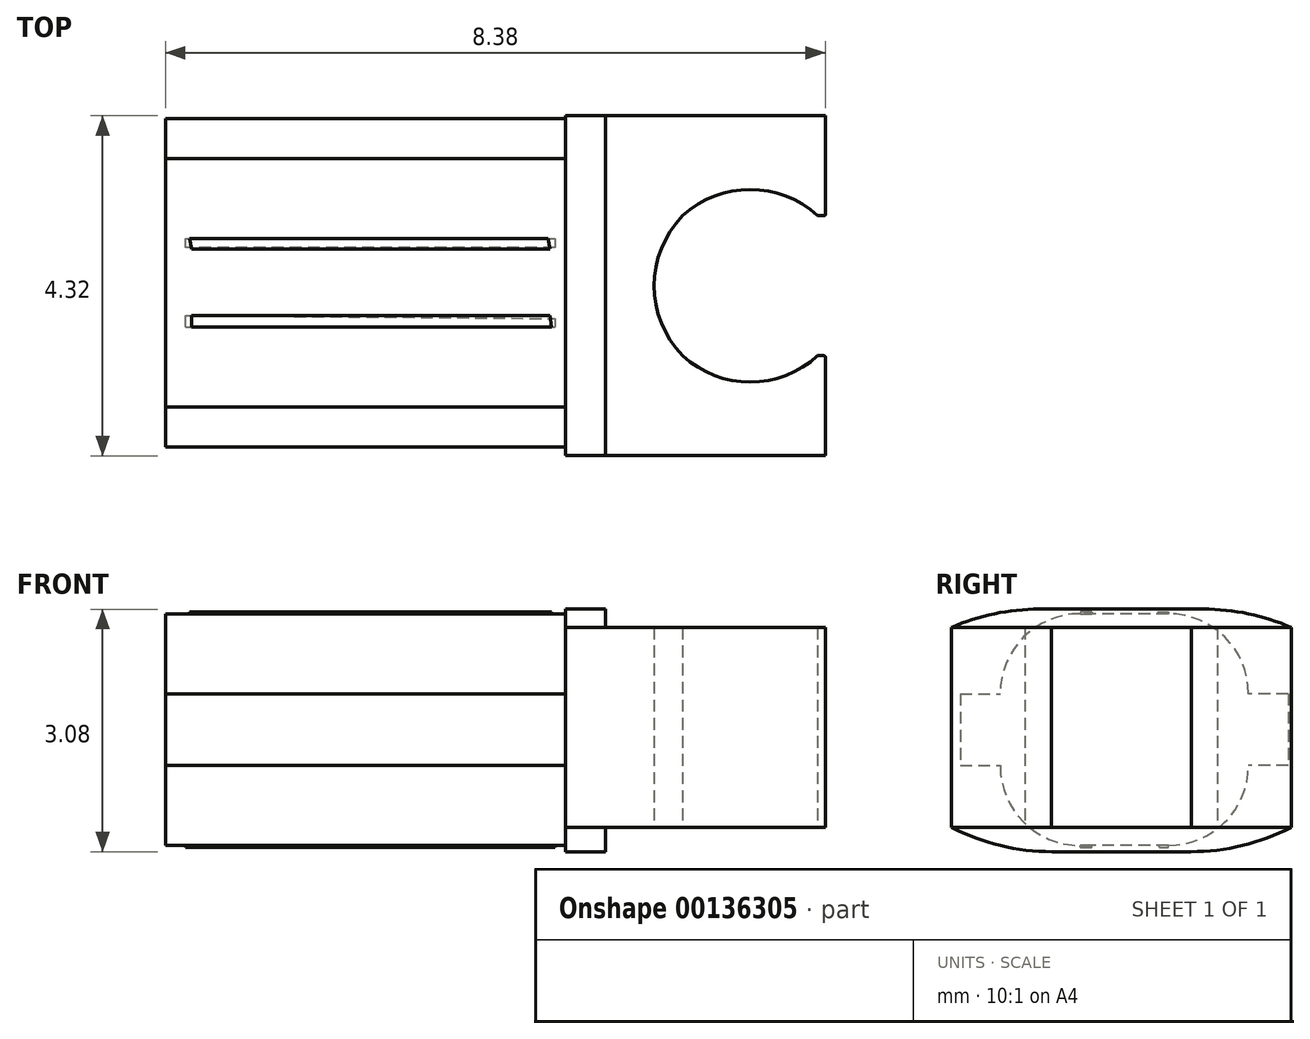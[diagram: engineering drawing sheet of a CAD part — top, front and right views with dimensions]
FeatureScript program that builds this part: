
annotation { "Feature Type Name" : "Feature", "Feature Type Description" : "" }
export const myFeature = defineFeature(function(context is Context, id is Id, definition is map)
    precondition{}
    {
        {
            var Q0;
            Q0=qCreatedBy(makeId("Top.planeOp"),FACE);
            var sketch = newSketch(context, id + "F0", { "sketchPlane" : qUnion([Q0])});
            skLineSegment(sketch, "E0", {"start": v(-1.88, 2.16) * mm, "end": v(0.91, 2.16) * mm});
            skLineSegment(sketch, "E1", {"start": v(-1.88, -2.16) * mm, "end": v(0.91, -2.16) * mm});
            skLineSegment(sketch, "E2", {"start": v(-1.88, 2.16) * mm, "end": v(-1.88, -2.16) * mm});
            skArc(sketch, "E3", {"start": v(-0.9, 0.89) * mm, "mid": v(-1.26, 0) * mm, "end": v(-0.9, -0.89) * mm});
            skLineSegment(sketch, "E4", {"start": v(0.91, -2.16) * mm, "end": v(0.91, -0.89) * mm});
            skArc(sketch, "E5", {"start": v(0.81, 0.89) * mm, "mid": v(-0.04, 1.22) * mm, "end": v(-0.9, 0.89) * mm});
            skArc(sketch, "E6", {"start": v(-0.9, -0.89) * mm, "mid": v(-0.04, -1.22) * mm, "end": v(0.81, -0.89) * mm});
            skLineSegment(sketch, "E7", {"start": v(0.81, 0.89) * mm, "end": v(0.86, 0.89) * mm});
            skLineSegment(sketch, "E8", {"start": v(0.86, 0.89) * mm, "end": v(0.91, 0.89) * mm});
            skLineSegment(sketch, "E9", {"start": v(0.91, 2.16) * mm, "end": v(0.91, 0.89) * mm});
            skLineSegment(sketch, "E10", {"start": v(0.81, -0.89) * mm, "end": v(0.86, -0.89) * mm});
            skLineSegment(sketch, "E11", {"start": v(0.91, -0.89) * mm, "end": v(0.86, -0.89) * mm});
            skSolve(sketch);
        }
        {
            var Q0;
            Q0=makeQuery(id+"F0.imprint","IMPRINT",FACE,{"disambiguationData":[TD([[makeQuery(id+"F0.imprint","IMPRINT",EDGE,{"derivedFrom":sQuery(id+"F0.wireOp",EDGE,"E0")}),-1.0]])]});
            extrude(context, id + "F1", {"entities" : qUnion([Q0]), "endBound" : BoundingType.SYMMETRIC, "depth" : 2.54 * mm});
        }
        {
            var Q0;
            Q0=makeQuery(id+"F1.opExtrude","SWEPT_EDGE",EDGE,{"disambiguationData":[OSD([sQuery(id+"F0.wireOp",EDGE,"E8"),sQuery(id+"F0.wireOp",EDGE,"E9")])]});
            var Q1;
            Q1=makeQuery(id+"F1.opExtrude","SWEPT_EDGE",EDGE,{"disambiguationData":[OSD([sQuery(id+"F0.wireOp",EDGE,"E4"),sQuery(id+"F0.wireOp",EDGE,"E11")])]});
            fillet(context, id + "F2", {"entities" : qUnion([Q0, Q1]), "radius" : 0.03 * mm, "tangentPropagation" : true, "allowEdgeOverflow" : false});
        }
        {
            var Q0;
            Q0=makeQuery(id+"F1.opExtrude","SWEPT_FACE",FACE,{"disambiguationData":[OSD([sQuery(id+"F0.wireOp",EDGE,"E2")])]});
            var sketch = newSketch(context, id + "F3", { "sketchPlane" : qUnion([Q0])});
            skLineSegment(sketch, "E12", {"start": v(-2.16, 1.27) * mm, "end": v(-1.96, 1.5) * mm});
            skLineSegment(sketch, "E13", {"start": v(-1.96, 1.5) * mm, "end": v(1.86, 1.5) * mm});
            skLineSegment(sketch, "E14", {"start": v(1.86, 1.5) * mm, "end": v(2.16, 1.27) * mm});
            skLineSegment(sketch, "E15", {"start": v(-2.16, 1.27) * mm, "end": v(-2.16, -1.27) * mm});
            skLineSegment(sketch, "E16", {"start": v(-2.16, -1.27) * mm, "end": v(-1.95, -1.58) * mm});
            skLineSegment(sketch, "E17", {"start": v(-1.95, -1.58) * mm, "end": v(1.86, -1.58) * mm});
            skLineSegment(sketch, "E18", {"start": v(1.86, -1.58) * mm, "end": v(2.16, -1.27) * mm});
            skLineSegment(sketch, "E19", {"start": v(2.16, -1.27) * mm, "end": v(2.16, 1.27) * mm});
            skSolve(sketch);
        }
        {
            var Q0;
            Q0 = qSketchRegion(id + "F3", true);
            extrude(context, id + "F4", {"entities" : qUnion([Q0]), "operationType" : NewBodyOperationType.ADD, "depth" : 0.5 * mm});
        }
        {
            var Q0;
            Q0=makeQuery(id+"F4.opExtrude","SWEPT_EDGE",EDGE,{"disambiguationData":[OSD([sQuery(id+"F3.wireOp",EDGE,"E12"),sQuery(id+"F3.wireOp",EDGE,"E13")])]});
            var Q1;
            Q1=makeQuery(id+"F4.opExtrude","SWEPT_EDGE",EDGE,{"disambiguationData":[OSD([sQuery(id+"F3.wireOp",EDGE,"E13"),sQuery(id+"F3.wireOp",EDGE,"E14")])]});
            var Q2;
            Q2=makeQuery(id+"F4.opExtrude","SWEPT_EDGE",EDGE,{"disambiguationData":[OSD([sQuery(id+"F3.wireOp",EDGE,"E16"),sQuery(id+"F3.wireOp",EDGE,"E17")])]});
            var Q3;
            Q3=makeQuery(id+"F4.opExtrude","SWEPT_EDGE",EDGE,{"disambiguationData":[OSD([sQuery(id+"F3.wireOp",EDGE,"E17"),sQuery(id+"F3.wireOp",EDGE,"E18")])]});
            fillet(context, id + "F5", {"entities" : qUnion([Q0, Q1, Q2, Q3]), "radius" : 2.8 * mm, "tangentPropagation" : true, "allowEdgeOverflow" : false});
        }
        {
            var Q0;
            Q0=makeQuery(id+"F4.opExtrude","CAP_FACE",FACE,{"disambiguationData":[OSD([sQuery(id+"F3.wireOp",EDGE,"E12"),sQuery(id+"F3.wireOp",EDGE,"E13"),sQuery(id+"F3.wireOp",EDGE,"E14"),sQuery(id+"F3.wireOp",EDGE,"E15"),sQuery(id+"F3.wireOp",EDGE,"E16"),sQuery(id+"F3.wireOp",EDGE,"E17"),sQuery(id+"F3.wireOp",EDGE,"E18"),sQuery(id+"F3.wireOp",EDGE,"E19")])],"isStart":false});
            var sketch = newSketch(context, id + "F6", { "sketchPlane" : qUnion([Q0])});
            skLineSegment(sketch, "E20.bottom", {"start": v(-1.61, 1.44) * mm, "end": v(1.54, 1.44) * mm});
            skLineSegment(sketch, "E20.top", {"start": v(-1.61, -1.5) * mm, "end": v(1.54, -1.5) * mm});
            skLineSegment(sketch, "E20.left", {"start": v(-1.61, 1.44) * mm, "end": v(-1.61, -1.5) * mm});
            skLineSegment(sketch, "E20.right", {"start": v(1.54, 1.44) * mm, "end": v(1.54, -1.5) * mm});
            skSolve(sketch);
        }
        {
            var Q0;
            Q0 = qSketchRegion(id + "F6", true);
            extrude(context, id + "F7", {"entities" : qUnion([Q0]), "operationType" : NewBodyOperationType.ADD, "depth" : 5.08 * mm});
        }
        {
            var Q0;
            Q0=makeQuery(id+"F7.opExtrude","SWEPT_EDGE",EDGE,{"disambiguationData":[OSD([sQuery(id+"F3.wireOp",EDGE,"E12"),sQuery(id+"F3.wireOp",EDGE,"E13"),sQuery(id+"F3.wireOp",EDGE,"E14"),sQuery(id+"F3.wireOp",EDGE,"E15"),sQuery(id+"F3.wireOp",EDGE,"E16"),sQuery(id+"F3.wireOp",EDGE,"E17"),sQuery(id+"F3.wireOp",EDGE,"E18"),sQuery(id+"F3.wireOp",EDGE,"E19"),sQuery(id+"F6.wireOp",EDGE,"E20.bottom"),sQuery(id+"F6.wireOp",EDGE,"E20.left")])]});
            var Q1;
            Q1=makeQuery(id+"F7.opExtrude","SWEPT_EDGE",EDGE,{"disambiguationData":[OSD([sQuery(id+"F6.wireOp",EDGE,"E20.bottom"),sQuery(id+"F6.wireOp",EDGE,"E20.right")])]});
            var Q2;
            Q2=makeQuery(id+"F7.opExtrude","SWEPT_EDGE",EDGE,{"disambiguationData":[OSD([sQuery(id+"F6.wireOp",EDGE,"E20.top"),sQuery(id+"F6.wireOp",EDGE,"E20.left")])]});
            var Q3;
            Q3=makeQuery(id+"F7.opExtrude","SWEPT_EDGE",EDGE,{"disambiguationData":[OSD([sQuery(id+"F3.wireOp",EDGE,"E12"),sQuery(id+"F3.wireOp",EDGE,"E13"),sQuery(id+"F3.wireOp",EDGE,"E14"),sQuery(id+"F3.wireOp",EDGE,"E15"),sQuery(id+"F3.wireOp",EDGE,"E16"),sQuery(id+"F3.wireOp",EDGE,"E17"),sQuery(id+"F3.wireOp",EDGE,"E18"),sQuery(id+"F3.wireOp",EDGE,"E19"),sQuery(id+"F6.wireOp",EDGE,"E20.top"),sQuery(id+"F6.wireOp",EDGE,"E20.right")])]});
            fillet(context, id + "F8", {"entities" : qUnion([Q0, Q1, Q2, Q3]), "radius" : 1.02 * mm, "tangentPropagation" : true, "allowEdgeOverflow" : false});
        }
        {
            var Q0;
            Q0=makeQuery(id+"F7.opExtrude","SWEPT_FACE",FACE,{"disambiguationData":[OSD([sQuery(id+"F6.wireOp",EDGE,"E20.bottom")])]});
            var sketch = newSketch(context, id + "F9", { "sketchPlane" : qUnion([Q0])});
            skLineSegment(sketch, "E21", {"start": v(-2.58, 0.75) * mm, "end": v(-7.14, 0.75) * mm});
            skLineSegment(sketch, "E22", {"start": v(-7.14, 0.47) * mm, "end": v(-2.58, 0.47) * mm});
            skLineSegment(sketch, "E23", {"start": v(-2.58, -0.38) * mm, "end": v(-7.14, -0.38) * mm});
            skLineSegment(sketch, "E24", {"start": v(-7.14, -0.68) * mm, "end": v(-2.58, -0.68) * mm});
            skLineSegment(sketch, "E25", {"start": v(-7.14, 0.47) * mm, "end": v(-7.17, 0.6) * mm});
            skLineSegment(sketch, "E26", {"start": v(-7.17, 0.6) * mm, "end": v(-2.6, 0.6) * mm});
            skLineSegment(sketch, "E27", {"start": v(-2.6, 0.6) * mm, "end": v(-2.58, 0.47) * mm});
            skLineSegment(sketch, "E28", {"start": v(-7.14, -0.38) * mm, "end": v(-7.14, -0.52) * mm});
            skLineSegment(sketch, "E29", {"start": v(-7.14, -0.52) * mm, "end": v(-2.57, -0.52) * mm});
            skLineSegment(sketch, "E30", {"start": v(-2.57, -0.52) * mm, "end": v(-2.58, -0.38) * mm});
            skSolve(sketch);
        }
        {
            var Q0;
            Q0 = qSketchRegion(id + "F9", true);
            extrude(context, id + "F10", {"entities" : qUnion([Q0]), "operationType" : NewBodyOperationType.ADD, "depth" : 0.03 * mm});
        }
        {
            var Q0;
            Q0=makeQuery(id+"F7.opExtrude","SWEPT_FACE",FACE,{"disambiguationData":[OSD([sQuery(id+"F6.wireOp",EDGE,"E20.top")])]});
            var sketch = newSketch(context, id + "F11", { "sketchPlane" : qUnion([Q0])});
            skLineSegment(sketch, "E31", {"start": v(-2.52, 0.42) * mm, "end": v(-2.52, 0.52) * mm});
            skLineSegment(sketch, "E32", {"start": v(-2.52, 0.52) * mm, "end": v(-7.22, 0.52) * mm});
            skLineSegment(sketch, "E33", {"start": v(-7.22, 0.52) * mm, "end": v(-7.22, 0.38) * mm});
            skLineSegment(sketch, "E34", {"start": v(-7.22, 0.38) * mm, "end": v(-2.52, 0.42) * mm});
            skLineSegment(sketch, "E35", {"start": v(-2.52, -0.48) * mm, "end": v(-7.22, -0.48) * mm});
            skLineSegment(sketch, "E36", {"start": v(-7.22, -0.48) * mm, "end": v(-7.22, -0.6) * mm});
            skLineSegment(sketch, "E37", {"start": v(-7.22, -0.6) * mm, "end": v(-2.52, -0.6) * mm});
            skLineSegment(sketch, "E38", {"start": v(-2.52, -0.6) * mm, "end": v(-2.52, -0.48) * mm});
            skSolve(sketch);
        }
        {
            var Q0;
            Q0 = qSketchRegion(id + "F11", true);
            extrude(context, id + "F12", {"entities" : qUnion([Q0]), "operationType" : NewBodyOperationType.ADD, "depth" : 0.03 * mm});
        }
        {
            var Q0;
            Q0=makeQuery(id+"F7.opExtrude","SWEPT_FACE",FACE,{"disambiguationData":[OSD([sQuery(id+"F6.wireOp",EDGE,"E20.left")])]});
            var sketch = newSketch(context, id + "F13", { "sketchPlane" : qUnion([Q0])});
            skLineSegment(sketch, "E39", {"start": v(7.47, -0.49) * mm, "end": v(7.47, 0.43) * mm});
            skLineSegment(sketch, "E40", {"start": v(7.47, 0.43) * mm, "end": v(2.39, 0.43) * mm});
            skLineSegment(sketch, "E41", {"start": v(2.39, 0.43) * mm, "end": v(2.39, -0.49) * mm});
            skLineSegment(sketch, "E42", {"start": v(2.39, -0.49) * mm, "end": v(7.47, -0.49) * mm});
            skSolve(sketch);
        }
        {
            var Q0;
            Q0 = qSketchRegion(id + "F13", true);
            extrude(context, id + "F14", {"entities" : qUnion([Q0]), "operationType" : NewBodyOperationType.ADD, "depth" : 0.5 * mm});
        }
        {
            var Q0;
            Q0=makeQuery(id+"F7.opExtrude","SWEPT_FACE",FACE,{"disambiguationData":[OSD([sQuery(id+"F6.wireOp",EDGE,"E20.right")])]});
            var sketch = newSketch(context, id + "F15", { "sketchPlane" : qUnion([Q0])});
            skLineSegment(sketch, "E43", {"start": v(-2.39, -0.49) * mm, "end": v(-7.47, -0.49) * mm});
            skLineSegment(sketch, "E44", {"start": v(-7.47, -0.49) * mm, "end": v(-7.47, 0.43) * mm});
            skLineSegment(sketch, "E45", {"start": v(-7.47, 0.43) * mm, "end": v(-2.39, 0.43) * mm});
            skLineSegment(sketch, "E46", {"start": v(-2.39, 0.43) * mm, "end": v(-2.39, -0.49) * mm});
            skSolve(sketch);
        }
        {
            var Q0;
            Q0 = qSketchRegion(id + "F15", true);
            extrude(context, id + "F16", {"entities" : qUnion([Q0]), "operationType" : NewBodyOperationType.ADD, "depth" : 0.5 * mm});
        }
    });
